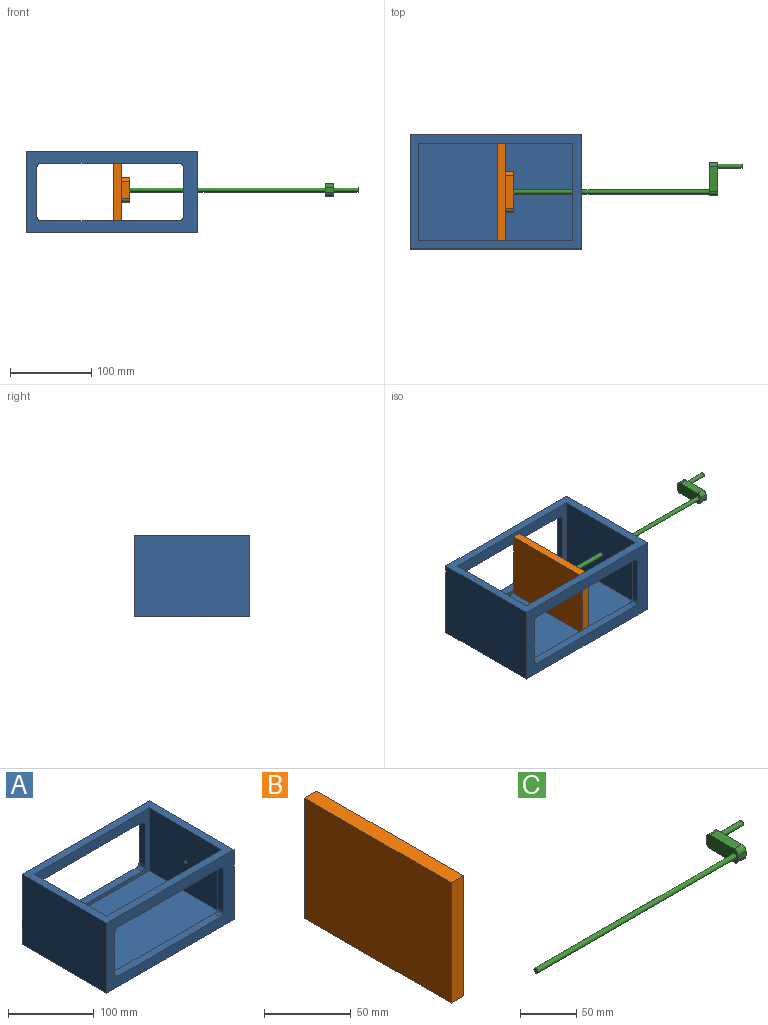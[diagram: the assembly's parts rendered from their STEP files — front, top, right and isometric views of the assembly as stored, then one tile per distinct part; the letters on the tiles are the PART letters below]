
ASSEMBLY  parts=3 mates=2
PART A: 28 faces, bbox 210x140x100 mm
  f0: plane 190x90mm, normal (0,1,0), area 4521.5mm2, adj f5,f6,f9,f10,f15,f16,f17,f18
  f1: plane 190x90mm, normal (0,-1,0), area 4521.5mm2, adj f5,f6,f9,f10,f11,f12,f13,f14
  f2: plane 210x100mm, normal (0,-1,0), area 8421.5mm2, adj f4,f7,f8,f9,f15,f16,f17,f18
  f3: plane 210x100mm, normal (0,1,0), area 8421.5mm2, adj f4,f7,f8,f9,f11,f12,f13,f14
  f4: plane 210x140mm, normal (0,0,-1), area 29400mm2, adj f2,f3,f7,f8
  f5: plane 120x90mm, normal (-1,0,0), area 10780.4mm2, adj f0,f1,f9,f10,f19
  f6: plane 120x90mm, normal (1,0,0), area 10800mm2, adj f0,f1,f9,f10
  f7: plane 140x100mm, normal (-1,0,0), area 14000mm2, adj f2,f3,f4,f9
  f8: plane 140x100mm, normal (1,0,0), area 13980.4mm2, adj f2,f3,f4,f9,f19
  f9: plane 210x140mm, normal (0,0,1), area 6600mm2, adj f0,f1,f2,f3,f5,f6,f7,f8
  f10: plane 190x120mm, normal (0,0,1), area 22800mm2, adj f0,f1,f5,f6
  f11: plane 60x10mm, normal (-1,0,0), area 600mm2, adj f1,f3,f26,f27
  f12: plane 170x10mm, normal (0,0,1), area 1700mm2, adj f1,f3,f25,f26
  f13: plane 60x10mm, normal (1,0,0), area 600mm2, adj f1,f3,f24,f25
  f14: plane 170x10mm, normal (0,0,-1), area 1700mm2, adj f1,f3,f24,f27
  f15: plane 170x10mm, normal (0,0,-1), area 1700mm2, adj f0,f2,f20,f22
  f16: plane 60x10mm, normal (1,0,0), area 600mm2, adj f0,f2,f20,f21
  f17: plane 170x10mm, normal (0,0,1), area 1700mm2, adj f0,f2,f21,f23
  f18: plane 60x10mm, normal (-1,0,0), area 600mm2, adj f0,f2,f22,f23
  f19: cylinder r=2.5mm len=10mm, axis (1,0,0), area 157.1mm2, adj f5,f8
  f20: cylinder r=5mm len=10mm, axis (0,1,0), area 78.5mm2, adj f0,f2,f15,f16
  f21: cylinder r=5mm len=10mm, axis (0,-1,0), area 78.5mm2, adj f0,f2,f16,f17
  f22: cylinder r=5mm len=10mm, axis (0,-1,0), area 78.5mm2, adj f0,f2,f15,f18
  f23: cylinder r=5mm len=10mm, axis (0,1,0), area 78.5mm2, adj f0,f2,f17,f18
  f24: cylinder r=5mm len=10mm, axis (0,1,0), area 78.5mm2, adj f1,f3,f13,f14
  f25: cylinder r=5mm len=10mm, axis (0,-1,0), area 78.5mm2, adj f1,f3,f12,f13
  f26: cylinder r=5mm len=10mm, axis (0,1,0), area 78.5mm2, adj f1,f3,f11,f12
  f27: cylinder r=5mm len=10mm, axis (0,-1,0), area 78.5mm2, adj f1,f3,f11,f14
PART B: 17 faces, bbox 20x120x85 mm
  f0: plane 120x10mm, normal (0,0,-1), area 1200mm2, adj f1,f3,f4,f5
  f1: plane 85x10mm, normal (0,1,0), area 850mm2, adj f0,f2,f4,f5
  f2: plane 120x10mm, normal (0,0,1), area 1200mm2, adj f1,f3,f4,f5
  f3: plane 85x10mm, normal (0,-1,0), area 850mm2, adj f0,f2,f4,f5
  f4: plane 120x85mm, normal (1,0,0), area 8721.5mm2, adj f0,f1,f2,f3,f6,f7,f8,f9
  f5: plane 120x85mm, normal (-1,0,0), area 10200mm2, adj f0,f1,f2,f3
  f6: plane 20x10mm, normal (0,1,0), area 200mm2, adj f4,f10,f13,f16
  f7: plane 40x10mm, normal (0,0,1), area 400mm2, adj f4,f10,f13,f14
  f8: plane 20x10mm, normal (0,-1,0), area 200mm2, adj f4,f10,f14,f15
  f9: plane 40x10mm, normal (0,0,-1), area 400mm2, adj f4,f10,f15,f16
  f10: plane 50x30mm, normal (1,0,0), area 1458.9mm2, adj f6,f7,f8,f9,f11,f13,f14,f15
  f11: cylinder r=2.5mm len=10mm, axis (1,0,0), area 157.1mm2, adj f10,f12
  f12: plane 5x5mm, normal (1,0,0), area 19.6mm2, adj f11
  f13: cylinder r=5mm len=10mm, axis (1,0,0), area 78.5mm2, adj f4,f6,f7,f10
  f14: cylinder r=5mm len=10mm, axis (-1,0,0), area 78.5mm2, adj f4,f7,f8,f10
  f15: cylinder r=5mm len=10mm, axis (1,0,0), area 78.5mm2, adj f4,f8,f9,f10
  f16: cylinder r=5mm len=10mm, axis (-1,0,0), area 78.5mm2, adj f4,f6,f9,f10
PART C: 14 faces, bbox 290x40x15 mm
  f0: plane 30x10mm, normal (0,0,-1), area 300mm2, adj f4,f5,f6,f9
  f1: plane 10x5mm, normal (0,1,0), area 50mm2, adj f4,f5,f6,f7
  f2: plane 30x10mm, normal (0,0,1), area 300mm2, adj f4,f5,f7,f8
  f3: plane 10x5mm, normal (0,-1,0), area 50mm2, adj f4,f5,f8,f9
  f4: plane 40x15mm, normal (1,0,0), area 558.9mm2, adj f0,f1,f2,f3,f6,f7,f8,f9
  f5: plane 40x15mm, normal (-1,0,0), area 558.9mm2, adj f0,f1,f2,f3,f6,f7,f8,f9
  f6: cylinder r=5mm len=10mm, axis (1,0,0), area 78.5mm2, adj f0,f1,f4,f5
  f7: cylinder r=5mm len=10mm, axis (-1,0,0), area 78.5mm2, adj f1,f2,f4,f5
  f8: cylinder r=5mm len=10mm, axis (1,0,0), area 78.5mm2, adj f2,f3,f4,f5
  f9: cylinder r=5mm len=10mm, axis (-1,0,0), area 78.5mm2, adj f0,f3,f4,f5
  f10: cylinder r=2.5mm len=30mm, axis (-1,0,0), area 471.2mm2, adj f4,f11
  f11: plane 5x5mm, normal (1,0,0), area 19.6mm2, adj f10
  f12: cylinder r=2.5mm len=250mm, axis (1,0,0), area 3927mm2, adj f5,f13
  f13: plane 5x5mm, normal (-1,0,0), area 19.6mm2, adj f12
PLACE A t=(-74.22,66.65,7.43)mm
PLACE B t=(-71.72,66.65,59.93)mm
PLACE C t=(188.28,82.42,59.93)mm
MATE cylindrical A.f19 <-> C.f12  axis (1,0,0) through (30.78,66.65,59.93)mm
MATE fastened C.f12 <-> B.f11  axis (-1,0,0) through (-61.72,66.65,59.93)mm
